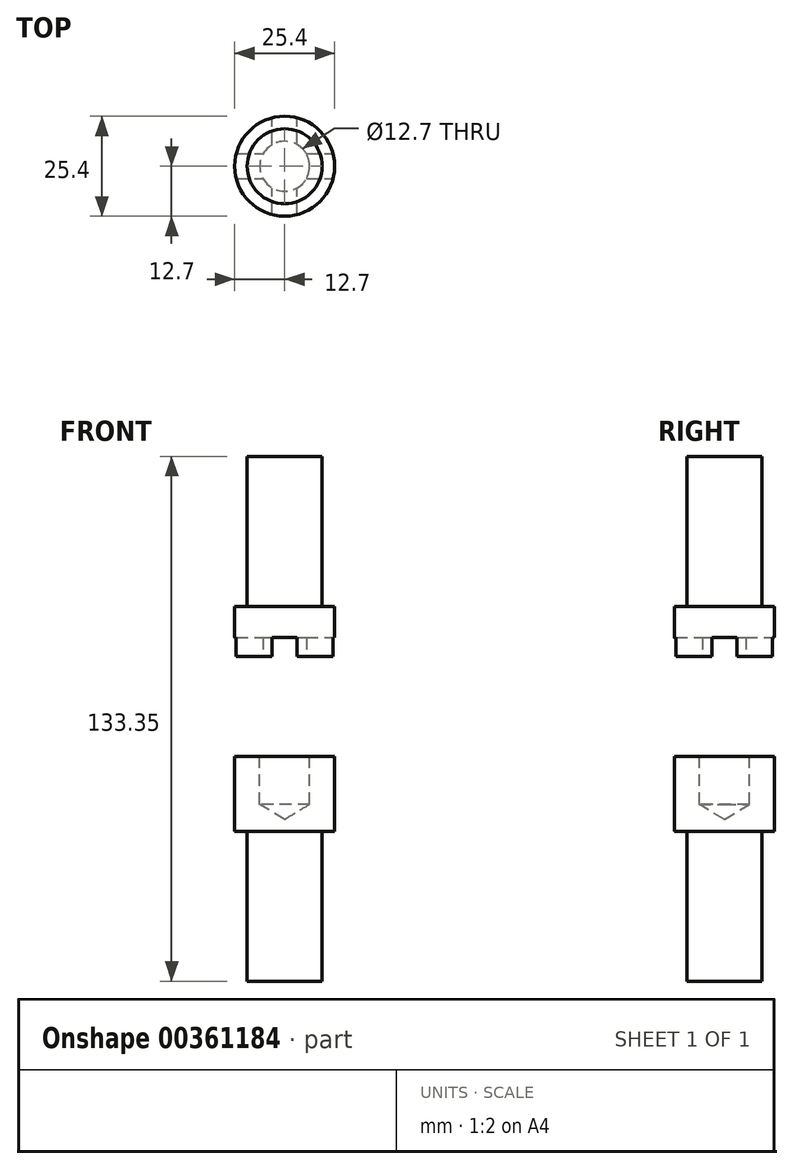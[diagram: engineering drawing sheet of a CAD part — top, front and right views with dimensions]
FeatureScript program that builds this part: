
annotation { "Feature Type Name" : "Feature", "Feature Type Description" : "" }
export const myFeature = defineFeature(function(context is Context, id is Id, definition is map)
    precondition{}
    {
        {
            var Q0;
            Q0=qCreatedBy(makeId("Front.planeOp"),FACE);
            var sketch = newSketch(context, id + "F0", { "sketchPlane" : qUnion([Q0])});
            skLineSegment(sketch, "E0", {"start": v(6.35, 0) * mm, "end": v(6.35, -12.19) * mm});
            skLineSegment(sketch, "E1", {"start": v(6.35, -12.19) * mm, "end": v(0, -16) * mm});
            skLineSegment(sketch, "E2", {"start": v(0, -16) * mm, "end": v(0, -57.15) * mm});
            skLineSegment(sketch, "E3", {"start": v(0, -57.15) * mm, "end": v(9.53, -57.15) * mm});
            skLineSegment(sketch, "E4", {"start": v(9.53, -57.15) * mm, "end": v(9.53, -19.05) * mm});
            skLineSegment(sketch, "E5", {"start": v(9.53, -19.05) * mm, "end": v(12.7, -19.05) * mm});
            skLineSegment(sketch, "E6", {"start": v(12.7, -19.05) * mm, "end": v(12.7, 0) * mm});
            skLineSegment(sketch, "E7", {"start": v(12.7, 0) * mm, "end": v(6.35, 0) * mm});
            skLineSegment(sketch, "E8", {"start": v(0, 32.51) * mm, "end": v(0, 14.86) * mm, "construction": true});
            skSolve(sketch);
        }
        {
            var Q0;
            Q0 = qSketchRegion(id + "F0", true);
            var Q1;
            Q1=sQuery(id+"F0.wireOp",EDGE,"E8");
            revolve(context, id + "F1", {"entities" : qUnion([Q0]), "axis" : qUnion([Q1]), "revolveType" : RevolveType.FULL});
        }
        {
            var Q0;
            Q0=qCreatedBy(makeId("Front.planeOp"),FACE);
            var sketch = newSketch(context, id + "F2", { "sketchPlane" : qUnion([Q0])});
            skLineSegment(sketch, "E9", {"start": v(0, 13.47) * mm, "end": v(0, 33.42) * mm, "construction": true});
            skLineSegment(sketch, "E10", {"start": v(0, 30.18) * mm, "end": v(6.35, 30.18) * mm});
            skLineSegment(sketch, "E11", {"start": v(6.35, 30.18) * mm, "end": v(6.35, 25.4) * mm});
            skLineSegment(sketch, "E12", {"start": v(6.35, 25.4) * mm, "end": v(12.7, 25.4) * mm});
            skLineSegment(sketch, "E13", {"start": v(12.7, 25.4) * mm, "end": v(12.7, 38.1) * mm});
            skLineSegment(sketch, "E14", {"start": v(12.7, 38.1) * mm, "end": v(9.52, 38.1) * mm});
            skLineSegment(sketch, "E15", {"start": v(9.53, 38.1) * mm, "end": v(9.53, 76.2) * mm});
            skLineSegment(sketch, "E16", {"start": v(9.52, 76.2) * mm, "end": v(0, 76.2) * mm});
            skLineSegment(sketch, "E17", {"start": v(0, 76.2) * mm, "end": v(0, 30.18) * mm});
            skSolve(sketch);
        }
        {
            var Q0;
            Q0 = qSketchRegion(id + "F2", true);
            var Q1;
            Q1=sQuery(id+"F2.wireOp",EDGE,"E9");
            revolve(context, id + "F3", {"entities" : qUnion([Q0]), "axis" : qUnion([Q1]), "revolveType" : RevolveType.FULL});
        }
        {
            var Q0;
            Q0=qCreatedBy(makeId("Right.planeOp"),FACE);
            var sketch = newSketch(context, id + "F4", { "sketchPlane" : qUnion([Q0])});
            skLineSegment(sketch, "E18.bottom", {"start": v(-3.18, 30.18) * mm, "end": v(3.17, 30.18) * mm});
            skLineSegment(sketch, "E18.top", {"start": v(-3.18, 25.4) * mm, "end": v(3.17, 25.4) * mm});
            skLineSegment(sketch, "E18.left", {"start": v(-3.18, 30.18) * mm, "end": v(-3.18, 25.4) * mm});
            skLineSegment(sketch, "E18.right", {"start": v(3.17, 30.18) * mm, "end": v(3.17, 25.4) * mm});
            skPoint(sketch, "E18.middle", {"position": v(0, 27.79) * mm});
            skSolve(sketch);
        }
        {
            var Q0;
            Q0 = qSketchRegion(id + "F4", true);
            extrude(context, id + "F5", {"entities" : qUnion([Q0]), "operationType" : NewBodyOperationType.REMOVE, "endBound" : BoundingType.THROUGH_ALL, "oppositeDirection" : true, "depth" : 25.4 * mm, "hasSecondDirection" : true, "secondDirectionBound" : SecondDirectionBoundingType.THROUGH_ALL, "secondDirectionOppositeDirection" : false, "secondDirectionDepth" : 25.4 * mm});
        }
        {
            var Q0;
            Q0=qCreatedBy(makeId("Front.planeOp"),FACE);
            var sketch = newSketch(context, id + "F6", { "sketchPlane" : qUnion([Q0])});
            skLineSegment(sketch, "E19.bottom", {"start": v(3.17, 30.18) * mm, "end": v(-3.18, 30.18) * mm});
            skLineSegment(sketch, "E19.top", {"start": v(3.17, 25.4) * mm, "end": v(-3.18, 25.4) * mm});
            skLineSegment(sketch, "E19.left", {"start": v(3.17, 30.18) * mm, "end": v(3.17, 25.4) * mm});
            skLineSegment(sketch, "E19.right", {"start": v(-3.18, 30.18) * mm, "end": v(-3.18, 25.4) * mm});
            skPoint(sketch, "E19.middle", {"position": v(0, 27.79) * mm});
            skSolve(sketch);
        }
        {
            var Q0;
            Q0 = qSketchRegion(id + "F6", true);
            extrude(context, id + "F7", {"entities" : qUnion([Q0]), "operationType" : NewBodyOperationType.REMOVE, "endBound" : BoundingType.THROUGH_ALL, "depth" : 25.4 * mm, "hasSecondDirection" : true, "secondDirectionBound" : SecondDirectionBoundingType.THROUGH_ALL, "secondDirectionOppositeDirection" : true, "secondDirectionDepth" : 25.4 * mm});
        }
    });
